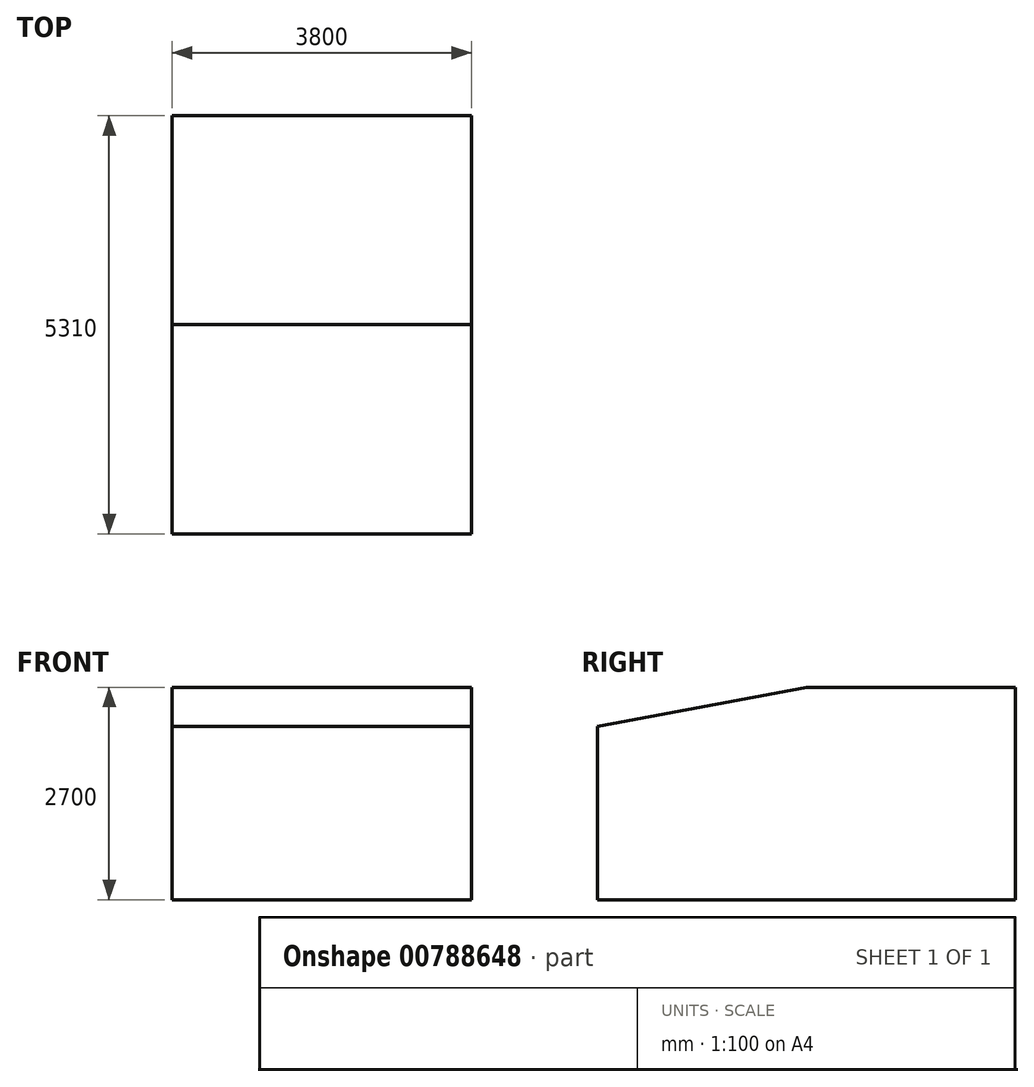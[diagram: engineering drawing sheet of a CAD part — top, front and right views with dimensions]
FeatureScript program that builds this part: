
annotation { "Feature Type Name" : "Feature", "Feature Type Description" : "" }
export const myFeature = defineFeature(function(context is Context, id is Id, definition is map)
    precondition{}
    {
        {
            var Q0;
            Q0=qCreatedBy(makeId("Top.planeOp"),FACE);
            var sketch = newSketch(context, id + "F0", { "sketchPlane" : qUnion([Q0])});
            skLineSegment(sketch, "E0.bottom", {"start": v(1900, 2655) * mm, "end": v(-1900, 2655) * mm});
            skLineSegment(sketch, "E0.top", {"start": v(1900, -2655) * mm, "end": v(-1900, -2655) * mm});
            skLineSegment(sketch, "E0.left", {"start": v(1900, 2655) * mm, "end": v(1900, -2655) * mm});
            skLineSegment(sketch, "E0.right", {"start": v(-1900, 2655) * mm, "end": v(-1900, -2655) * mm});
            skPoint(sketch, "E0.middle", {"position": v(0, 0) * mm});
            skSolve(sketch);
        }
        {
            var Q0;
            Q0=makeQuery(id+"F0.imprint","IMPRINT",FACE,{"disambiguationData":[TD([[makeQuery(id+"F0.imprint","IMPRINT",EDGE,{"derivedFrom":sQuery(id+"F0.wireOp",EDGE,"E0.bottom")}),1.0]])]});
            extrude(context, id + "F1", {"entities" : qUnion([Q0]), "depth" : 2700 * mm, "offsetDistance" : 25 * mm});
        }
        {
            var Q0;
            Q0=makeQuery(id+"F1.opExtrude","SWEPT_FACE",FACE,{"disambiguationData":[OSD([sQuery(id+"F0.wireOp",EDGE,"E0.right")])]});
            var sketch = newSketch(context, id + "F2", { "sketchPlane" : qUnion([Q0])});
            skLineSegment(sketch, "E1", {"start": v(0, 2700) * mm, "end": v(2655, 2200) * mm});
            skLineSegment(sketch, "E2", {"start": v(0, 2700) * mm, "end": v(-2655, 2160.07) * mm});
            skLineSegment(sketch, "E3", {"start": v(2655, 2200) * mm, "end": v(-2655, 1350) * mm});
            skSolve(sketch);
        }
        {
            var Q0;
            {var subQ0=sQuery(id+"F2.wireOp",EDGE,"E1");Q0=makeQuery(id+"F2.imprint","IMPRINT",FACE,{"disambiguationData":[TD([[makeQuery(id+"F2.imprint","IMPRINT",EDGE,{"derivedFrom":subQ0}),1.0]])]});}
            extrude(context, id + "F3", {"entities" : qUnion([Q0]), "operationType" : NewBodyOperationType.REMOVE, "endBound" : BoundingType.UP_TO_NEXT, "oppositeDirection" : true, "depth" : 25 * mm, "offsetDistance" : 25 * mm});
        }
    });
